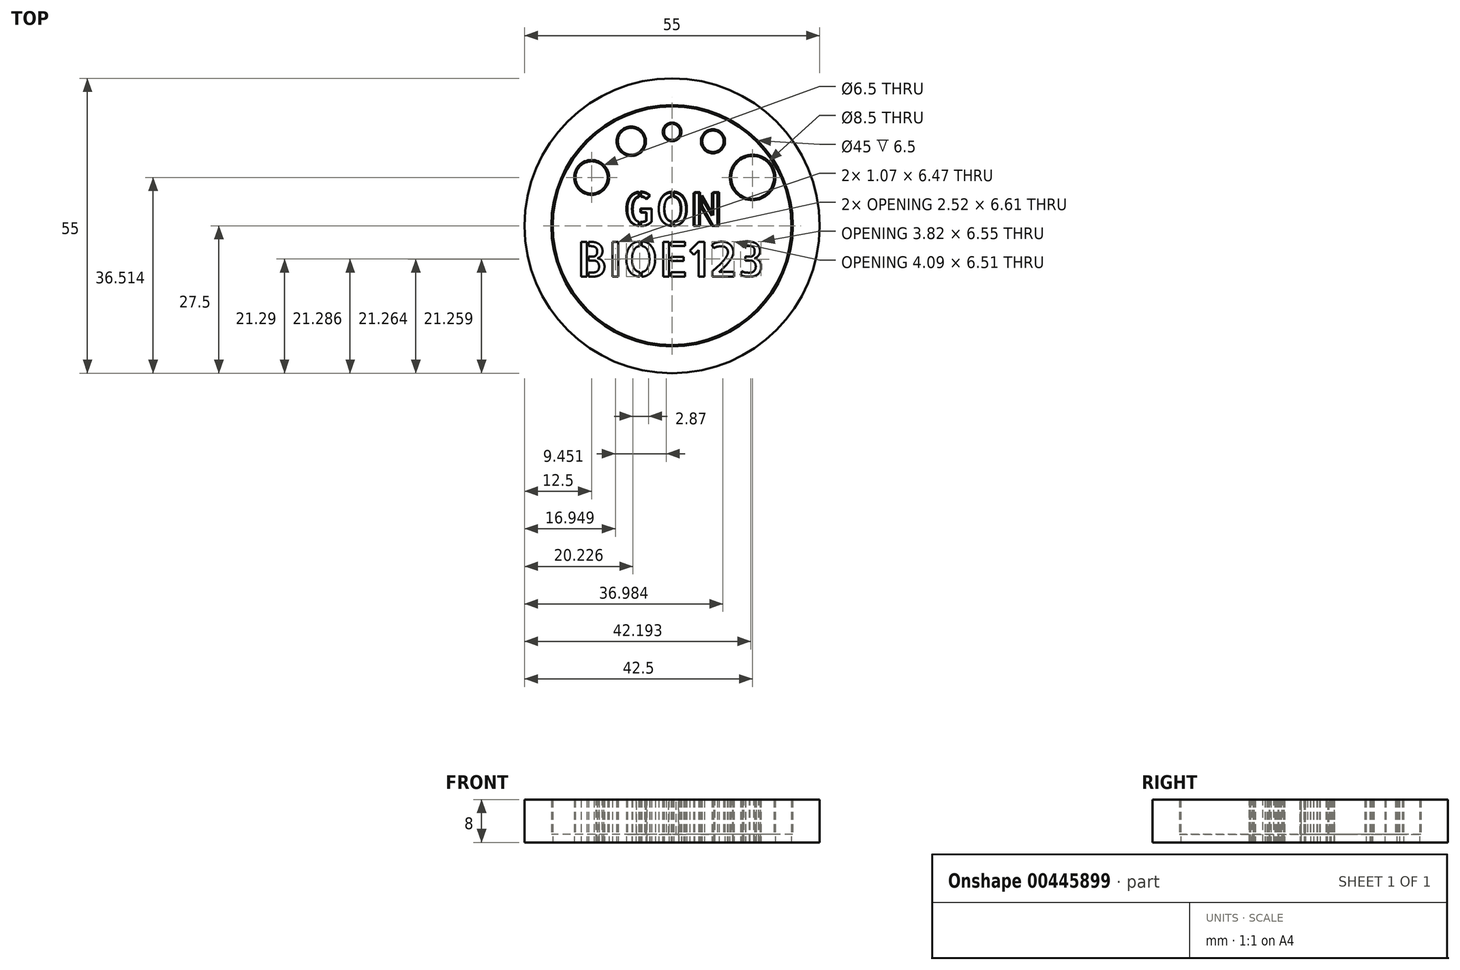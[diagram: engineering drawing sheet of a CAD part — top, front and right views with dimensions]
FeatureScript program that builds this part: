
annotation { "Feature Type Name" : "Feature", "Feature Type Description" : "" }
export const myFeature = defineFeature(function(context is Context, id is Id, definition is map)
    precondition{}
    {
        {
            var Q0;
            Q0=qCreatedBy(makeId("Top.planeOp"),FACE);
            var sketch = newSketch(context, id + "F0", { "sketchPlane" : qUnion([Q0])});
            skCircle(sketch, "E0", {"center": v(0, 0) * mm, "radius": 22.5 * mm});
            skCircle(sketch, "E1", {"center": v(0, 0) * mm, "radius": 27.5 * mm});
            skSolve(sketch);
        }
        {
            var Q0;
            Q0=makeQuery(id+"F0.imprint","IMPRINT",FACE,{"disambiguationData":[TD([[makeQuery(id+"F0.imprint","IMPRINT",EDGE,{"derivedFrom":sQuery(id+"F0.wireOp",EDGE,"E0")}),-1.0]])]});
            extrude(context, id + "F1", {"entities" : qUnion([Q0]), "depth" : 8 * mm});
        }
        {
            var Q0;
            Q0=qCreatedBy(makeId("Top.planeOp"),FACE);
            var sketch = newSketch(context, id + "F2", { "sketchPlane" : qUnion([Q0])});
            skCircle(sketch, "E2", {"center": v(0, 0) * mm, "radius": 27.5 * mm});
            skSolve(sketch);
        }
        {
            var Q0;
            Q0 = qSketchRegion(id + "F2", true);
            extrude(context, id + "F3", {"entities" : qUnion([Q0]), "operationType" : NewBodyOperationType.ADD, "depth" : 1.5 * mm});
        }
        {
            var Q0;
            Q0=qCreatedBy(makeId("Top.planeOp"),FACE);
            var sketch = newSketch(context, id + "F4", { "sketchPlane" : qUnion([Q0])});
            skText(sketch, "E3", { "text": "GON", "fontName": "AllertaStencil-Regular.ttf"});
            const initialGuessF4  = {"E3": [-0.009, 0, 1, 0, 0.00611]};
            skSetInitialGuess(sketch, initialGuessF4);
            skSolve(sketch);
        }
        {
            var Q0;
            Q0 = qSketchRegion(id + "F4", true);
            extrude(context, id + "F5", {"entities" : qUnion([Q0]), "operationType" : NewBodyOperationType.ADD, "depth" : 8 * mm});
        }
        {
            var Q0;
            Q0=qCreatedBy(makeId("Top.planeOp"),FACE);
            var sketch = newSketch(context, id + "F6", { "sketchPlane" : qUnion([Q0])});
            skCircle(sketch, "E4", {"center": v(-15, 9.01) * mm, "radius": 3 * mm});
            skCircle(sketch, "E5", {"center": v(-7.61, 15.76) * mm, "radius": 2.5 * mm});
            skCircle(sketch, "E6", {"center": v(0, 17.5) * mm, "radius": 1.5 * mm});
            skCircle(sketch, "E7", {"center": v(15, 9.01) * mm, "radius": 4 * mm});
            skCircle(sketch, "E8", {"center": v(7.61, 15.76) * mm, "radius": 2 * mm});
            skSolve(sketch);
        }
        {
            var Q0;
            Q0 = qSketchRegion(id + "F6", true);
            extrude(context, id + "F7", {"entities" : qUnion([Q0]), "operationType" : NewBodyOperationType.ADD, "depth" : 8 * mm});
        }
        {
            var Q0;
            Q0=qCreatedBy(makeId("Top.planeOp"),FACE);
            var sketch = newSketch(context, id + "F8", { "sketchPlane" : qUnion([Q0])});
            skCircle(sketch, "E9", {"center": v(0, 0) * mm, "radius": 22.25 * mm});
            skCircle(sketch, "E10", {"center": v(-15, 9.01) * mm, "radius": 3.25 * mm});
            skCircle(sketch, "E11", {"center": v(-7.61, 15.76) * mm, "radius": 2.75 * mm});
            skCircle(sketch, "E12", {"center": v(0, 17.5) * mm, "radius": 1.75 * mm});
            skCircle(sketch, "E13", {"center": v(7.61, 15.76) * mm, "radius": 2.25 * mm});
            skCircle(sketch, "E14", {"center": v(15, 9.01) * mm, "radius": 4.25 * mm});
            skText(sketch, "E15", { "text": "GON", "fontName": "AllertaStencil-Regular.ttf"});
            skText(sketch, "E16", { "text": "BIOE123", "fontName": "AllertaStencil-Regular.ttf"});
            const initialGuessF8  = {"E15": [-0.00918, 0, 1, 0, 0.00628], "E16": [-0.0178, -0.00947, 1, 0, 0.00647]};
            skSetInitialGuess(sketch, initialGuessF8);
            skSolve(sketch);
        }
        {
            var Q0;
            Q0=makeQuery(id+"F8.imprint","IMPRINT",FACE,{"disambiguationData":[TD([[makeQuery(id+"F8.imprint","IMPRINT",EDGE,{"derivedFrom":sQuery(id+"F8.wireOp",EDGE,"E9")}),1.0]])]});
            extrude(context, id + "F9", {"entities" : qUnion([Q0]), "depth" : 8 * mm});
        }
        {
            var Q0;
            Q0=makeQuery(id+"F8.imprint","IMPRINT",FACE,{"disambiguationData":[TD([[makeQuery(id+"F8.imprint","IMPRINT",EDGE,{"derivedFrom":sQuery(id+"F8.wireOp",EDGE,"E10")}),1.0]])]});
            var Q1;
            Q1=makeQuery(id+"F8.imprint","IMPRINT",FACE,{"disambiguationData":[TD([[makeQuery(id+"F8.imprint","IMPRINT",EDGE,{"derivedFrom":sQuery(id+"F8.wireOp",EDGE,"E11")}),1.0]])]});
            var Q2;
            Q2=makeQuery(id+"F8.imprint","IMPRINT",FACE,{"disambiguationData":[TD([[makeQuery(id+"F8.imprint","IMPRINT",EDGE,{"derivedFrom":sQuery(id+"F8.wireOp",EDGE,"E12")}),1.0]])]});
            var Q3;
            Q3=makeQuery(id+"F8.imprint","IMPRINT",FACE,{"disambiguationData":[TD([[makeQuery(id+"F8.imprint","IMPRINT",EDGE,{"derivedFrom":sQuery(id+"F8.wireOp",EDGE,"E13")}),1.0]])]});
            var Q4;
            Q4=makeQuery(id+"F8.imprint","IMPRINT",FACE,{"disambiguationData":[TD([[makeQuery(id+"F8.imprint","IMPRINT",EDGE,{"derivedFrom":sQuery(id+"F8.wireOp",EDGE,"E14")}),1.0]])]});
            extrude(context, id + "F10", {"entities" : qUnion([Q0, Q1, Q2, Q3, Q4]), "operationType" : NewBodyOperationType.REMOVE, "oppositeDirection" : true, "depth" : 8 * mm});
        }
    });
